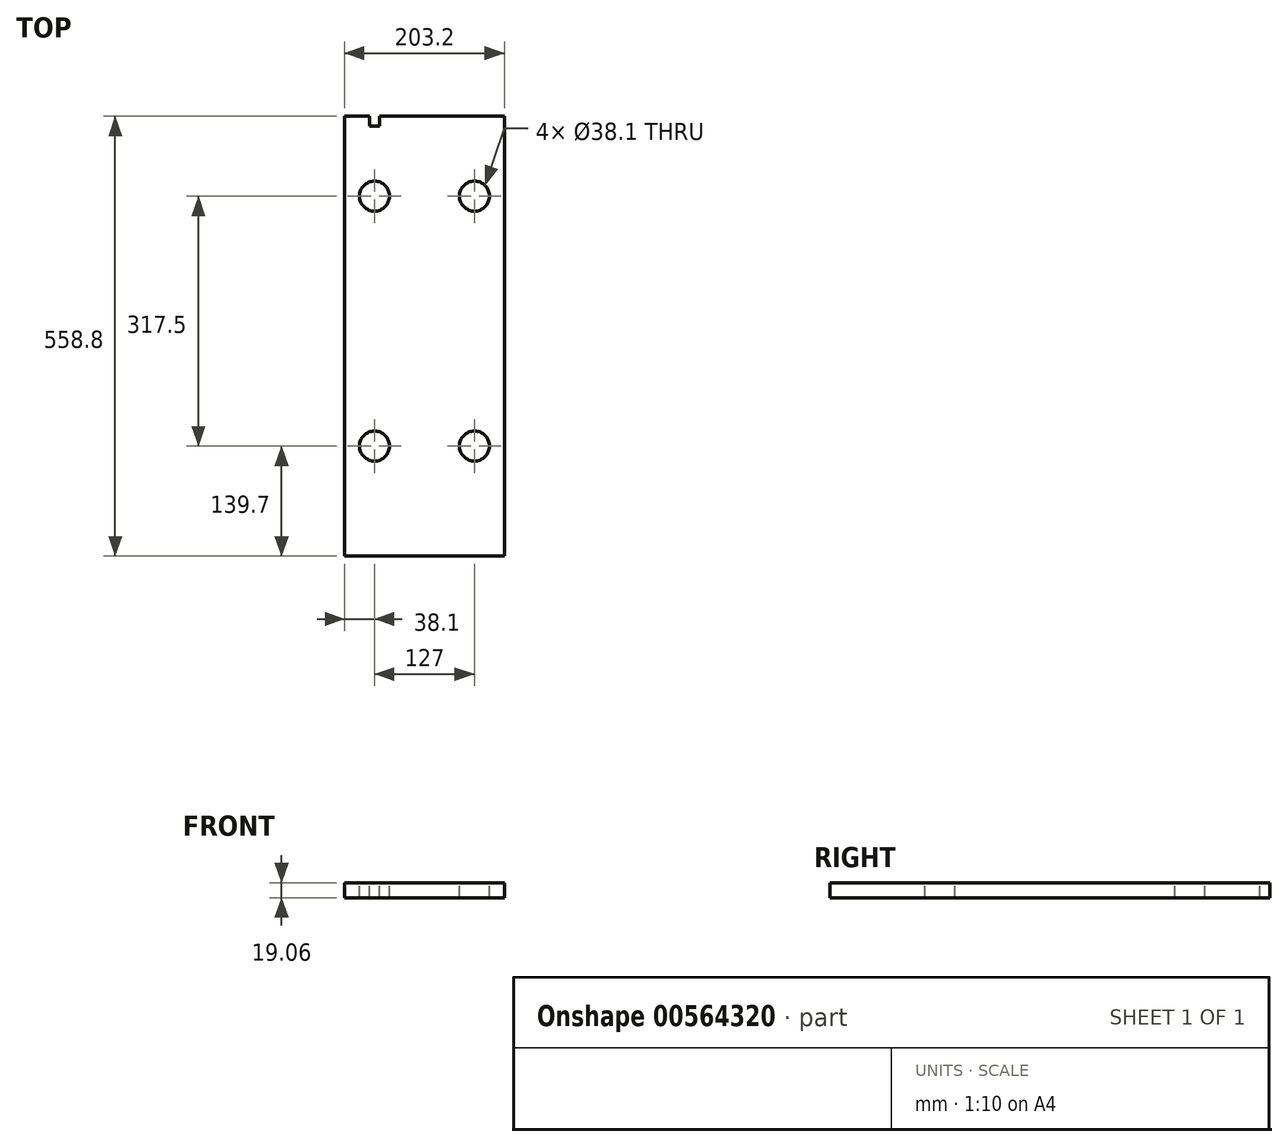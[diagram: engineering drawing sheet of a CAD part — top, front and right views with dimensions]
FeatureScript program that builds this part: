
annotation { "Feature Type Name" : "Feature", "Feature Type Description" : "" }
export const myFeature = defineFeature(function(context is Context, id is Id, definition is map)
    precondition{}
    {
        {
            var Q0;
            Q0=qCreatedBy(makeId("Front.planeOp"),FACE);
            var sketch = newSketch(context, id + "F0", { "sketchPlane" : qUnion([Q0])});
            skLineSegment(sketch, "E0.bottom", {"start": v(-101.6, 9.53) * mm, "end": v(101.6, 9.53) * mm});
            skLineSegment(sketch, "E0.top", {"start": v(-101.6, -9.53) * mm, "end": v(101.6, -9.53) * mm});
            skLineSegment(sketch, "E0.left", {"start": v(-101.6, 9.53) * mm, "end": v(-101.6, -9.53) * mm});
            skLineSegment(sketch, "E0.right", {"start": v(101.6, 9.53) * mm, "end": v(101.6, -9.53) * mm});
            skPoint(sketch, "E0.middle", {"position": v(0, 0) * mm});
            skSolve(sketch);
        }
        {
            var Q0;
            Q0=qSketchRegion(id+"F0",true);
            extrude(context, id + "F1", {"entities" : qUnion([Q0]), "depth" : 558.8 * mm, "offsetDistance" : 25.4 * mm});
        }
        {
            var Q0;
            Q0=makeQuery(id+"F1.opExtrude","SWEPT_FACE",FACE,{"disambiguationData":[OSD([sQuery(id+"F0.wireOp",EDGE,"E0.bottom")])]});
            var sketch = newSketch(context, id + "F2", { "sketchPlane" : qUnion([Q0])});
            skLineSegment(sketch, "E1", {"start": v(0, 0) * mm, "end": v(0, -627.02) * mm, "construction": true});
            skPoint(sketch, "E1.endSnap0", {"position": v(0, -558.8) * mm});
            skCircle(sketch, "E2", {"center": v(-63.5, -101.6) * mm, "radius": 19.05 * mm});
            skCircle(sketch, "E3", {"center": v(63.5, -101.6) * mm, "radius": 19.05 * mm});
            skCircle(sketch, "E4", {"center": v(-63.5, -419.1) * mm, "radius": 19.05 * mm});
            skCircle(sketch, "E5", {"center": v(63.5, -419.1) * mm, "radius": 19.05 * mm});
            skLineSegment(sketch, "E6.bottom", {"start": v(-69.85, 0) * mm, "end": v(-57.15, 0) * mm});
            skLineSegment(sketch, "E6.top", {"start": v(-69.85, -12.7) * mm, "end": v(-57.15, -12.7) * mm});
            skLineSegment(sketch, "E6.left", {"start": v(-69.85, 0) * mm, "end": v(-69.85, -12.7) * mm});
            skLineSegment(sketch, "E6.right", {"start": v(-57.15, 0) * mm, "end": v(-57.15, -12.7) * mm});
            skSolve(sketch);
        }
        {
            var Q0;
            Q0=qSketchRegion(id+"F2",true);
            extrude(context, id + "F3", {"entities" : qUnion([Q0]), "operationType" : NewBodyOperationType.REMOVE, "oppositeDirection" : true, "depth" : 25.4 * mm, "offsetDistance" : 25.4 * mm});
        }
    });
